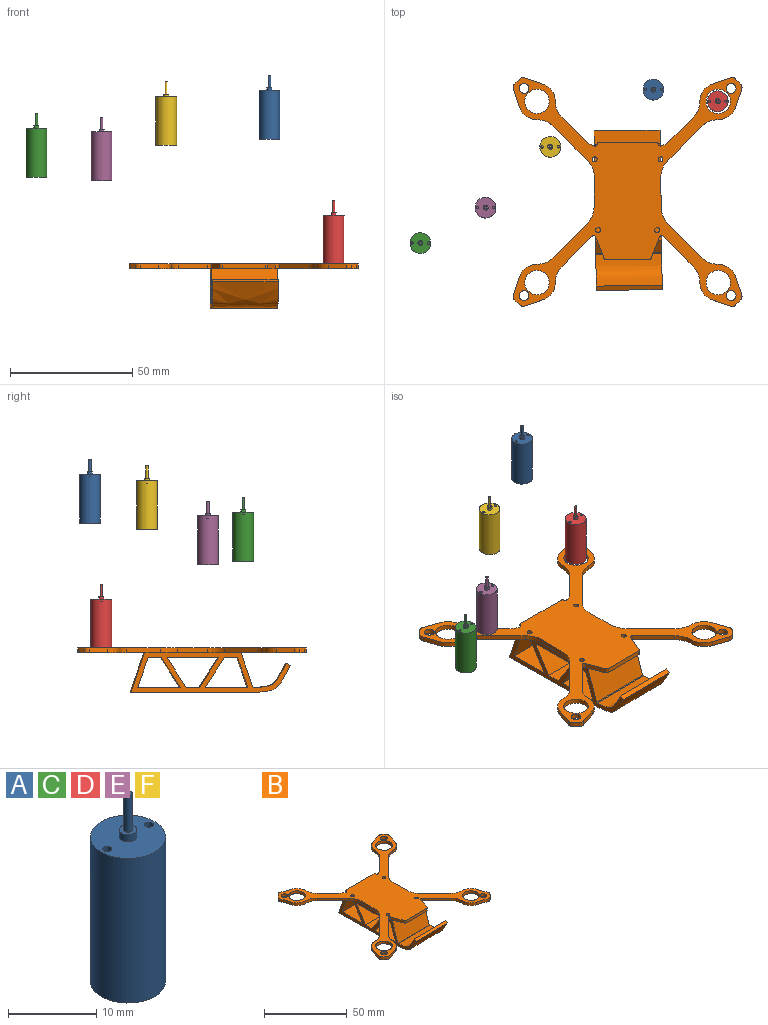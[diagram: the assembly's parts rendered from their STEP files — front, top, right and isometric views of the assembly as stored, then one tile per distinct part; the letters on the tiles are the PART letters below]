
ASSEMBLY  parts=6 mates=1
PART A: 11 faces, bbox 8.5x8.5x26 mm
  f0: plane 8.5x8.5mm, normal (0,0,1), area 52mm2, adj f1,f6,f7,f9
  f1: cylinder r=1mm len=2mm, axis (0,0,-1), area 6.3mm2, adj f0,f2
  f2: plane 2x2mm, normal (0,0,1), area 2.4mm2, adj f1,f3
  f3: cylinder r=0.5mm len=5mm, axis (0,0,-1), area 15.7mm2, adj f2,f4
  f4: plane 1x1mm, normal (0,0,1), area 0.8mm2, adj f3
  f5: plane 8.5x8.5mm, normal (0,0,-1), area 56.7mm2, adj f6
  f6: cylinder r=4.25mm len=20mm, axis (0,0,-1), area 534.1mm2, adj f0,f5
  f7: cylinder r=0.5mm len=1mm, axis (0,0,1), area 3.1mm2, adj f0,f8
  f8: plane 1x1mm, normal (0,0,1), area 0.8mm2, adj f7
  f9: cylinder r=0.5mm len=1mm, axis (0,0,1), area 3.1mm2, adj f0,f10
  f10: plane 1x1mm, normal (0,0,1), area 0.8mm2, adj f9
PART B: 110 faces, bbox 93.7x93.7x18.2 mm
  f0: plane 40.67x33.12mm, normal (0,0,-1), area 257.9mm2, adj f14,f15,f16,f17,f18,f19,f20,f21
  f1: plane 25.09x0.95mm, normal (0,0,-1), area 19.6mm2, adj f41,f42,f43,f44,f45,f83
  f2: plane 93.73x33.76mm, normal (0,0,-1), area 531.4mm2, adj f4,f5,f6,f7,f8,f45,f46,f47
  f3: plane 41.07x33.43mm, normal (0,0,-1), area 261.6mm2, adj f27,f28,f29,f30,f31,f32,f33,f34
  f4: plane 7.46x2.53mm, normal (0.32,-0.95,0), area 15.8mm2, adj f2,f5,f77,f80
  f5: cylinder r=7.5mm len=7.1mm, axis (0,0,-1), area 18.7mm2, adj f2,f4,f6,f80
  f6: cylinder r=9.56mm len=6.75mm, axis (0,0,-1), area 15mm2, adj f2,f5,f7,f80
  f7: plane 12.22x12.22mm, normal (0.71,-0.71,0), area 34.6mm2, adj f2,f6,f8,f80
  f8: cylinder r=1mm len=2mm, axis (0,0,-1), area 4mm2, adj f2,f7,f9,f80,f105
  f9: plane 8.48x3.23mm, normal (-0.93,-0.36,0), area 18.1mm2, adj f8,f10,f80,f81,f105
  f10: cylinder r=1mm len=2mm, axis (0,0,-1), area 2.4mm2, adj f9,f11,f80,f81
  f11: plane 17.62x2mm, normal (0,-1,0), area 35.2mm2, adj f10,f12,f80,f81
  f12: cylinder r=1mm len=2mm, axis (0,0,-1), area 2.4mm2, adj f11,f13,f80,f81
  f13: plane 8.48x3.23mm, normal (0.93,-0.36,0), area 18.1mm2, adj f12,f14,f80,f81,f106
  f14: cylinder r=1mm len=2mm, axis (0,0,-1), area 4mm2, adj f0,f13,f15,f80,f106
  f15: plane 12.22x12.22mm, normal (-0.71,-0.71,0), area 34.6mm2, adj f0,f14,f16,f80
  f16: cylinder r=9.56mm len=6.75mm, axis (0,0,-1), area 15mm2, adj f0,f15,f17,f80
  f17: cylinder r=7.5mm len=7.1mm, axis (0,0,-1), area 18.7mm2, adj f0,f16,f18,f80
  f18: plane 7.46x2.53mm, normal (-0.32,-0.95,0), area 15.8mm2, adj f0,f17,f19,f80
  f19: cylinder r=2mm len=2.06mm, axis (0,0,-1), area 4.5mm2, adj f0,f18,f20,f80
  f20: plane 2.05x2.05mm, normal (0.71,-0.71,0), area 5.8mm2, adj f0,f19,f21,f80
  f21: cylinder r=2mm len=2.06mm, axis (0,0,-1), area 4.5mm2, adj f0,f20,f22,f80
  f22: plane 7.46x2.53mm, normal (0.95,0.32,0), area 15.8mm2, adj f0,f21,f23,f80
  f23: cylinder r=7.5mm len=7.1mm, axis (0,0,-1), area 18.7mm2, adj f0,f22,f24,f80
  f24: cylinder r=9.56mm len=6.75mm, axis (0,0,-1), area 15mm2, adj f0,f23,f25,f80
  f25: plane 13.69x13.69mm, normal (0.71,0.71,0), area 38.7mm2, adj f0,f24,f26,f80
  f26: cylinder r=10mm len=6.95mm, axis (0,0,-1), area 15.5mm2, adj f0,f25,f27,f80
  f27: plane 65.32x18.25mm, normal (1,0.01,0), area 352.9mm2, adj f0,f3,f26,f28,f80,f83,f84,f85
  f28: cylinder r=10mm len=7.2mm, axis (0,0,-1), area 16mm2, adj f3,f27,f29,f80
  f29: plane 13.85x13.85mm, normal (0.71,-0.71,0), area 39.2mm2, adj f3,f28,f30,f80
  f30: cylinder r=9.56mm len=6.75mm, axis (0,0,-1), area 15mm2, adj f3,f29,f31,f80
  f31: cylinder r=7.5mm len=7.1mm, axis (0,0,-1), area 18.7mm2, adj f3,f30,f32,f80
  f32: plane 7.46x2.53mm, normal (0.95,-0.32,0), area 15.8mm2, adj f3,f31,f33,f80
  f33: cylinder r=2mm len=2.06mm, axis (0,0,-1), area 4.5mm2, adj f3,f32,f34,f80
  f34: plane 2.05x2.05mm, normal (0.71,0.71,0), area 5.8mm2, adj f3,f33,f35,f80
  f35: cylinder r=2mm len=2.06mm, axis (0,0,-1), area 4.5mm2, adj f3,f34,f36,f80
  f36: plane 7.46x2.53mm, normal (-0.32,0.95,0), area 15.8mm2, adj f3,f35,f37,f80
  f37: cylinder r=7.5mm len=7.1mm, axis (0,0,-1), area 18.7mm2, adj f3,f36,f38,f80
  f38: cylinder r=9.56mm len=6.75mm, axis (0,0,-1), area 15mm2, adj f3,f37,f39,f80
  f39: plane 9.06x9.06mm, normal (-0.71,0.71,0), area 25.6mm2, adj f3,f38,f40,f80
  f40: cylinder r=10mm len=3.96mm, axis (0,0,-1), area 9.4mm2, adj f3,f39,f41,f80
  f41: cylinder r=1mm len=2mm, axis (0,0,-1), area 3.8mm2, adj f1,f3,f40,f42,f80,f107
  f42: cylinder r=0.78mm len=2mm, axis (0,0,-1), area 1.8mm2, adj f1,f41,f43,f80
  f43: plane 23.5x2mm, normal (0,1,0), area 47mm2, adj f1,f42,f44,f80
  f44: cylinder r=0.78mm len=2mm, axis (0,0,-1), area 2.2mm2, adj f1,f43,f45,f80
  f45: cylinder r=1mm len=2mm, axis (0,0,-1), area 3.8mm2, adj f1,f2,f44,f46,f80,f104
  f46: cylinder r=10mm len=3.96mm, axis (0,0,-1), area 9.4mm2, adj f2,f45,f47,f80
  f47: plane 9.06x9.06mm, normal (0.71,0.71,0), area 25.6mm2, adj f2,f46,f48,f80
  f48: cylinder r=9.56mm len=6.75mm, axis (0,0,-1), area 15mm2, adj f2,f47,f49,f80
  f49: cylinder r=7.5mm len=7.1mm, axis (0,0,-1), area 18.7mm2, adj f2,f48,f50,f80
  f50: plane 7.46x2.53mm, normal (0.32,0.95,0), area 15.8mm2, adj f2,f49,f51,f80
  f51: cylinder r=2mm len=2.06mm, axis (0,0,-1), area 4.5mm2, adj f2,f50,f52,f80
  f52: plane 2.05x2.05mm, normal (-0.71,0.71,0), area 5.8mm2, adj f2,f51,f53,f80
  f53: cylinder r=2mm len=2.06mm, axis (0,0,-1), area 4.5mm2, adj f2,f52,f54,f80
  f54: plane 7.46x2.53mm, normal (-0.95,-0.32,0), area 15.8mm2, adj f2,f53,f55,f80
  f55: cylinder r=7.5mm len=7.1mm, axis (0,0,-1), area 18.7mm2, adj f2,f54,f56,f80
  f56: cylinder r=9.56mm len=6.75mm, axis (0,0,-1), area 15mm2, adj f2,f55,f57,f80
  f57: plane 13.85x13.85mm, normal (-0.71,-0.71,0), area 39.2mm2, adj f2,f56,f58,f80
  f58: cylinder r=10mm len=7.2mm, axis (0,0,-1), area 16mm2, adj f2,f57,f59,f80
  f59: plane 11.98x2mm, normal (-1,0.01,0), area 24mm2, adj f2,f58,f60,f80
  f60: cylinder r=10mm len=6.95mm, axis (0,0,-1), area 15.5mm2, adj f2,f59,f61,f80
  f61: plane 13.69x13.69mm, normal (-0.71,0.71,0), area 38.7mm2, adj f2,f60,f62,f80
  f62: cylinder r=9.56mm len=6.75mm, axis (0,0,-1), area 15mm2, adj f2,f61,f63,f80
  f63: cylinder r=7.5mm len=7.1mm, axis (0,0,-1), area 18.7mm2, adj f2,f62,f64,f80
  f64: plane 7.46x2.53mm, normal (-0.95,0.32,0), area 15.8mm2, adj f2,f63,f65,f80
  f65: cylinder r=2mm len=2.06mm, axis (0,0,-1), area 4.5mm2, adj f2,f64,f66,f80
  f66: plane 2.05x2.05mm, normal (-0.71,-0.71,0), area 5.8mm2, adj f2,f65,f77,f80
  f67: cylinder r=5mm len=10mm, axis (0,0,-1), area 62.8mm2, adj f2,f80
  f68: cylinder r=5mm len=10mm, axis (0,0,-1), area 62.8mm2, adj f2,f80
  f69: cylinder r=2mm len=4mm, axis (0,0,-1), area 25.1mm2, adj f0,f80
  f70: cylinder r=1mm len=2mm, axis (0,0,-1), area 12.6mm2, adj f3,f80,f102
  f71: cylinder r=1mm len=2mm, axis (0,0,-1), area 12.6mm2, adj f80,f108
  f72: cylinder r=1mm len=2mm, axis (0,0,-1), area 12.6mm2, adj f2,f80,f103
  f73: cylinder r=2mm len=4mm, axis (0,0,-1), area 25.1mm2, adj f2,f80
  f74: cylinder r=2mm len=4mm, axis (0,0,-1), area 25.1mm2, adj f3,f80
  f75: cylinder r=5mm len=10mm, axis (0,0,-1), area 62.8mm2, adj f0,f80
  f76: cylinder r=2mm len=4mm, axis (0,0,-1), area 25.1mm2, adj f2,f80
  f77: cylinder r=2mm len=2.06mm, axis (0,0,-1), area 4.5mm2, adj f2,f4,f66,f80
  f78: cylinder r=1mm len=2mm, axis (0,0,-1), area 12.6mm2, adj f80,f109
  f79: cylinder r=5mm len=10mm, axis (0,0,-1), area 62.8mm2, adj f3,f80
  f80: plane 93.73x93.73mm, normal (0,0,1), area 2292.7mm2, adj f4,f5,f6,f7,f8,f9,f10,f11
  f81: plane 24.85x7.85mm, normal (0,0,-1), area 168.5mm2, adj f9,f10,f11,f12,f13,f101
  f82: plane 65.32x16.25mm, normal (-1,-0.01,0), area 328.8mm2, adj f2,f83,f84,f85,f86,f87,f88,f89
  f83: plane 27.07x16.25mm, normal (-0.01,0.95,0.33), area 464mm2, adj f1,f27,f82,f96,f104,f107
  f84: plane 27.07x5.8mm, normal (0,0,1), area 147.4mm2, adj f27,f82,f87,f89
  f85: plane 27.22x17.79mm, normal (0,0,1), area 471.3mm2, adj f27,f82,f90,f92
  f86: plane 27.1x12.25mm, normal (0.01,-0.84,-0.54), area 392mm2, adj f27,f82,f93,f95
  f87: plane 27.1x12.25mm, normal (0.01,-0.84,0.54), area 392mm2, adj f27,f82,f84,f88
  f88: plane 27.26x21.39mm, normal (0,0,-1), area 568.5mm2, adj f27,f82,f87,f89
  f89: plane 27.1x12.25mm, normal (-0.01,0.84,0.54), area 392mm2, adj f27,f82,f84,f88
  f90: plane 27.05x12.25mm, normal (0.01,-0.95,-0.33), area 349.8mm2, adj f27,f82,f85,f91
  f91: plane 27.07x5.77mm, normal (0,0,-1), area 146.7mm2, adj f27,f82,f90,f92
  f92: plane 27.1x12.25mm, normal (-0.01,0.84,-0.54), area 392mm2, adj f27,f82,f85,f91
  f93: plane 27.07x5.77mm, normal (0,0,-1), area 146.7mm2, adj f27,f82,f86,f94
  f94: plane 27.05x12.25mm, normal (-0.01,0.95,-0.33), area 349.8mm2, adj f27,f82,f93,f95
  f95: plane 27.22x17.79mm, normal (0,0,1), area 471.3mm2, adj f27,f82,f86,f94
  f96: plane 50.98x27.63mm, normal (0,0,-1), area 1367.5mm2, adj f27,f82,f83,f97
  f97: extruded ~27.18x15.02mm, area 540.5mm2, adj f27,f82,f96,f98
  f98: plane 27.02x2.11mm, normal (0.01,-0.47,0.88), area 54mm2, adj f27,f82,f97,f99
  f99: extruded ~27.16x13.31mm, area 483.5mm2, adj f27,f82,f98,f100
  f100: plane 27.01x0.89mm, normal (0,0,1), area 14.9mm2, adj f27,f82,f99,f101
  f101: plane 27.06x14.25mm, normal (0.01,-0.95,0.33), area 406.9mm2, adj f27,f81,f82,f100,f105,f106
  f102: plane 2x1.01mm, normal (0,0,1), area 1.6mm2, adj f27,f70
  f103: plane 2x1.01mm, normal (0,0,1), area 1.6mm2, adj f72,f82
  f104: plane 1x0.6mm, normal (0,0,1), area 0.4mm2, adj f45,f82,f83
  f105: plane 1.84x0.74mm, normal (0,0,1), area 0.7mm2, adj f8,f9,f82,f101
  f106: plane 1.92x1.43mm, normal (0,0,1), area 1.9mm2, adj f13,f14,f27,f101
  f107: plane 0.93x0.93mm, normal (0,0,1), area 0.6mm2, adj f27,f41,f83
  f108: plane 2x2mm, normal (0,0,1), area 3.1mm2, adj f71
  f109: plane 2x2mm, normal (0,0,1), area 3.1mm2, adj f78
PART C: same geometry as A
PART D: same geometry as A
PART E: same geometry as A
PART F: same geometry as A
PLACE A t=(30.67,68.65,75.42)mm
PLACE B t=(19.7,26.84,14.7)mm
PLACE C t=(-64.79,5.83,59.8)mm
PLACE D t=(57.01,63.97,24.31)mm
PLACE E t=(-38.06,20.34,58.41)mm
PLACE F t=(-11.59,45.23,72.82)mm
MATE pin_slot D.f1 <-> B.f31  axis (0,0,-1) through (56.62,63.97,16.7)mm
